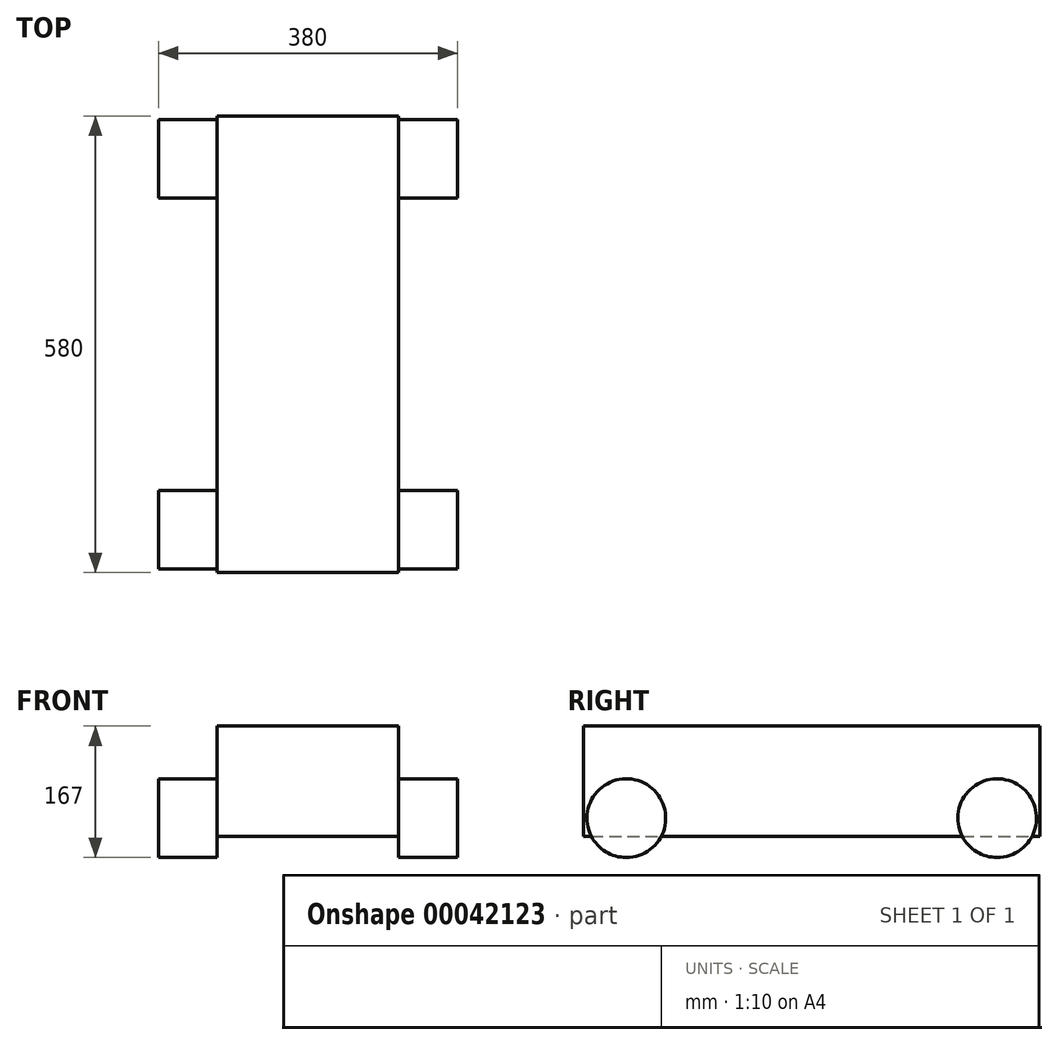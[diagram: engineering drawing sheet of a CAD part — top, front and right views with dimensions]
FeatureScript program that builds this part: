
annotation { "Feature Type Name" : "Feature", "Feature Type Description" : "" }
export const myFeature = defineFeature(function(context is Context, id is Id, definition is map)
    precondition{}
    {
        {
            var Q0;
            Q0=qCreatedBy(makeId("Front.planeOp"),FACE);
            var sketch = newSketch(context, id + "F0", { "sketchPlane" : qUnion([Q0])});
            skLineSegment(sketch, "E0.bottom", {"start": v(-127.07, 72.46) * mm, "end": v(103.2, 72.46) * mm});
            skLineSegment(sketch, "E0.top", {"start": v(-127.07, -67.54) * mm, "end": v(103.2, -67.54) * mm});
            skLineSegment(sketch, "E0.left", {"start": v(-127.07, 72.46) * mm, "end": v(-127.07, -67.54) * mm});
            skLineSegment(sketch, "E0.right", {"start": v(103.2, 72.46) * mm, "end": v(103.2, -67.54) * mm});
            skSolve(sketch);
        }
        {
            var Q0;
            Q0 = qSketchRegion(id + "F0", true);
            extrude(context, id + "F1", {"entities" : qUnion([Q0]), "depth" : 580 * mm});
        }
        {
            var Q0;
            Q0=makeQuery(id+"F1.opExtrude","SWEPT_FACE",FACE,{"disambiguationData":[OSD([sQuery(id+"F0.wireOp",EDGE,"E0.left")])]});
            var sketch = newSketch(context, id + "F2", { "sketchPlane" : qUnion([Q0])});
            skCircle(sketch, "E1", {"center": v(54.5, -44.54) * mm, "radius": 50 * mm});
            skCircle(sketch, "E2", {"center": v(525.5, -44.54) * mm, "radius": 50 * mm});
            skSolve(sketch);
        }
        {
            var Q0;
            Q0 = qSketchRegion(id + "F2", true);
            extrude(context, id + "F3", {"entities" : qUnion([Q0]), "operationType" : NewBodyOperationType.ADD, "depth" : 74.87 * mm});
        }
        {
            var Q0;
            Q0=makeQuery(id+"F1.opExtrude","SWEPT_FACE",FACE,{"disambiguationData":[OSD([sQuery(id+"F0.wireOp",EDGE,"E0.right")])]});
            var sketch = newSketch(context, id + "F4", { "sketchPlane" : qUnion([Q0])});
            skCircle(sketch, "E3", {"center": v(-525.5, -44.54) * mm, "radius": 50 * mm});
            skCircle(sketch, "E4", {"center": v(-54.5, -44.54) * mm, "radius": 50 * mm});
            skSolve(sketch);
        }
        {
            var Q0;
            Q0 = qSketchRegion(id + "F4", true);
            extrude(context, id + "F5", {"entities" : qUnion([Q0]), "operationType" : NewBodyOperationType.ADD, "depth" : 74.87 * mm});
        }
    });
